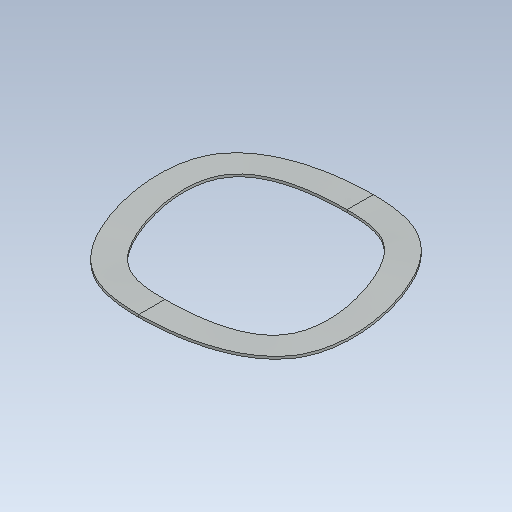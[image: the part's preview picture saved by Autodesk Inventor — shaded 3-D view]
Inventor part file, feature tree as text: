
AUTODESK INVENTOR PART (.ipt)
format: ipt  version: 2020 (Build 240168000, 168)  size: 124,416 bytes
history: native  units: in
note: dims shown in document units (in); Inventor stores cm internally (conversion verified against a paired STEP export)
features: loft x1
ambient origin geometry x8: Origin, YZ Plane, XZ Plane, XY Plane, X Axis, Y Axis, Z Axis, Center Point
bodies: Solid1 (feature_tree)
feature tree (1):
  loft  "Loft1"
